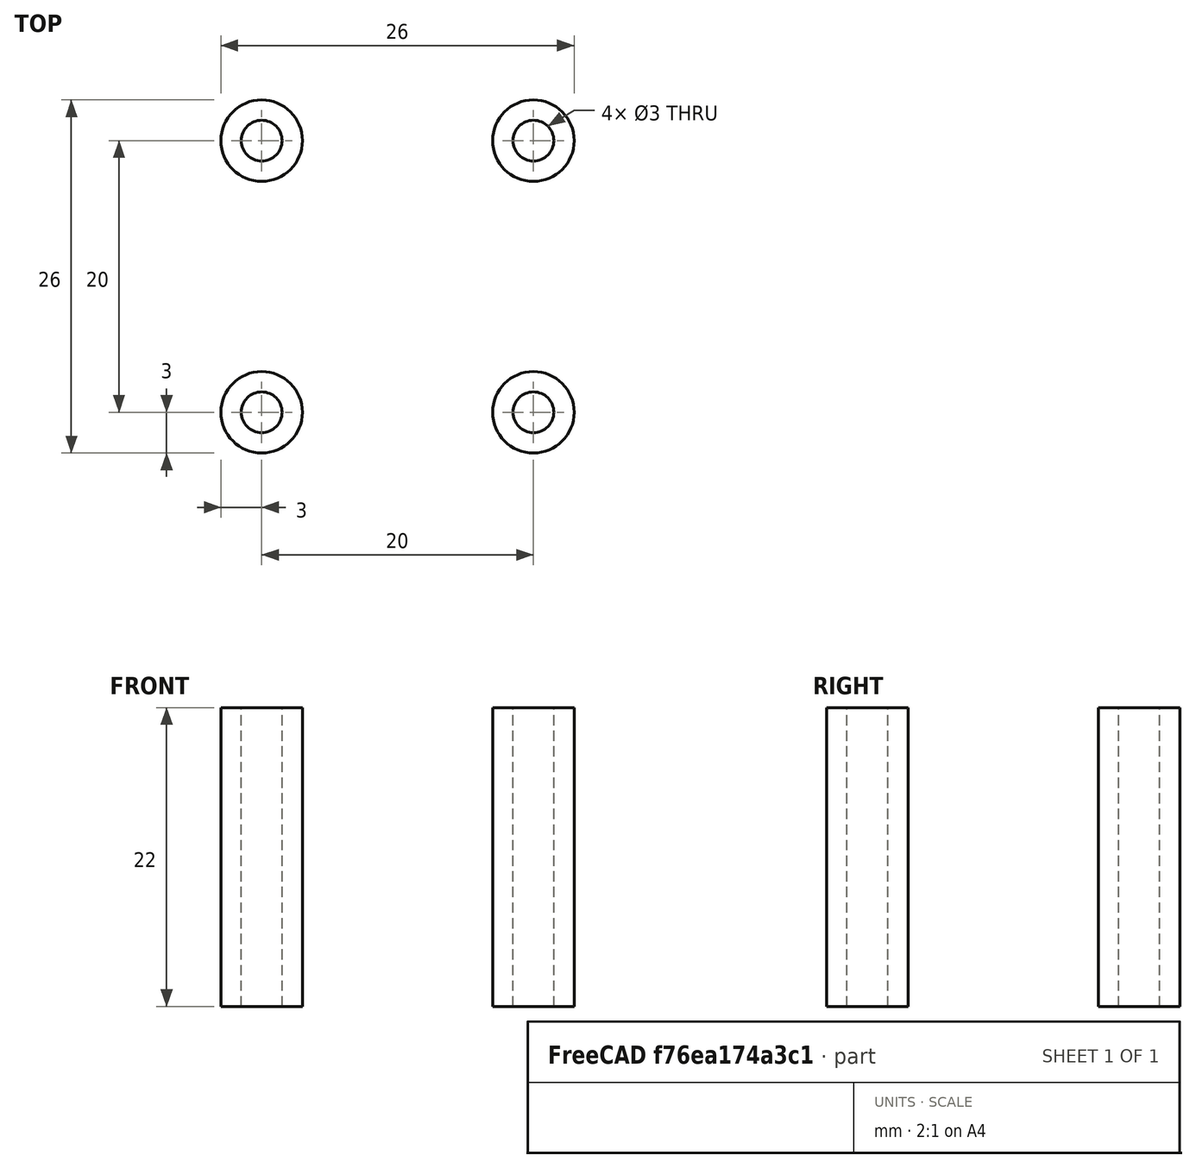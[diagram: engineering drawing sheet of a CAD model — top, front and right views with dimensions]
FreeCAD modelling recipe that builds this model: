
FCSTD DOCUMENT  (FreeCAD 0.17R13541 (Git))
Label: new poles
License: All rights reserved
LicenseURL: http://en.wikipedia.org/wiki/All_rights_reserved
objects: Part::Cylinder×8, Part::Cut×4
note: 12 computed .brp shape members not serialized (recipe doc carries the construction recipe); baked Part::Feature solids carry a one-line shape summary decoded from their .brp

FEATURE [Part::Cylinder] Cylinder
  Angle = 360
  AttacherType = Attacher::AttachEngine3D
  Height = 22
  Radius = 3
FEATURE [Part::Cylinder] Cylinder001
  Angle = 360
  AttacherType = Attacher::AttachEngine3D
  Height = 22
  Radius = 1.5
FEATURE [Part::Cut] Cut
  Base = -> Cylinder
  Tool = -> Cylinder001
FEATURE [Part::Cylinder] Cylinder002
  Angle = 360
  AttacherType = Attacher::AttachEngine3D
  Height = 22
  Radius = 3
FEATURE [Part::Cylinder] Cylinder003
  Angle = 360
  AttacherType = Attacher::AttachEngine3D
  Height = 22
  Radius = 1.5
FEATURE [Part::Cut] Cut001
  Base = -> Cylinder002
  Placement = pos=(0,20,0) rot=(0,0,1;0rad)
  Tool = -> Cylinder003
FEATURE [Part::Cylinder] Cylinder004
  Angle = 360
  AttacherType = Attacher::AttachEngine3D
  Height = 22
  Radius = 3
FEATURE [Part::Cylinder] Cylinder005
  Angle = 360
  AttacherType = Attacher::AttachEngine3D
  Height = 22
  Radius = 1.5
FEATURE [Part::Cut] Cut002
  Base = -> Cylinder004
  Placement = pos=(20,20,0) rot=(0,0,1;0rad)
  Tool = -> Cylinder005
FEATURE [Part::Cylinder] Cylinder006
  Angle = 360
  AttacherType = Attacher::AttachEngine3D
  Height = 22
  Radius = 3
FEATURE [Part::Cylinder] Cylinder007
  Angle = 360
  AttacherType = Attacher::AttachEngine3D
  Height = 22
  Radius = 1.5
FEATURE [Part::Cut] Cut003
  Base = -> Cylinder006
  Placement = pos=(20,0,0) rot=(0,0,1;0rad)
  Tool = -> Cylinder007
